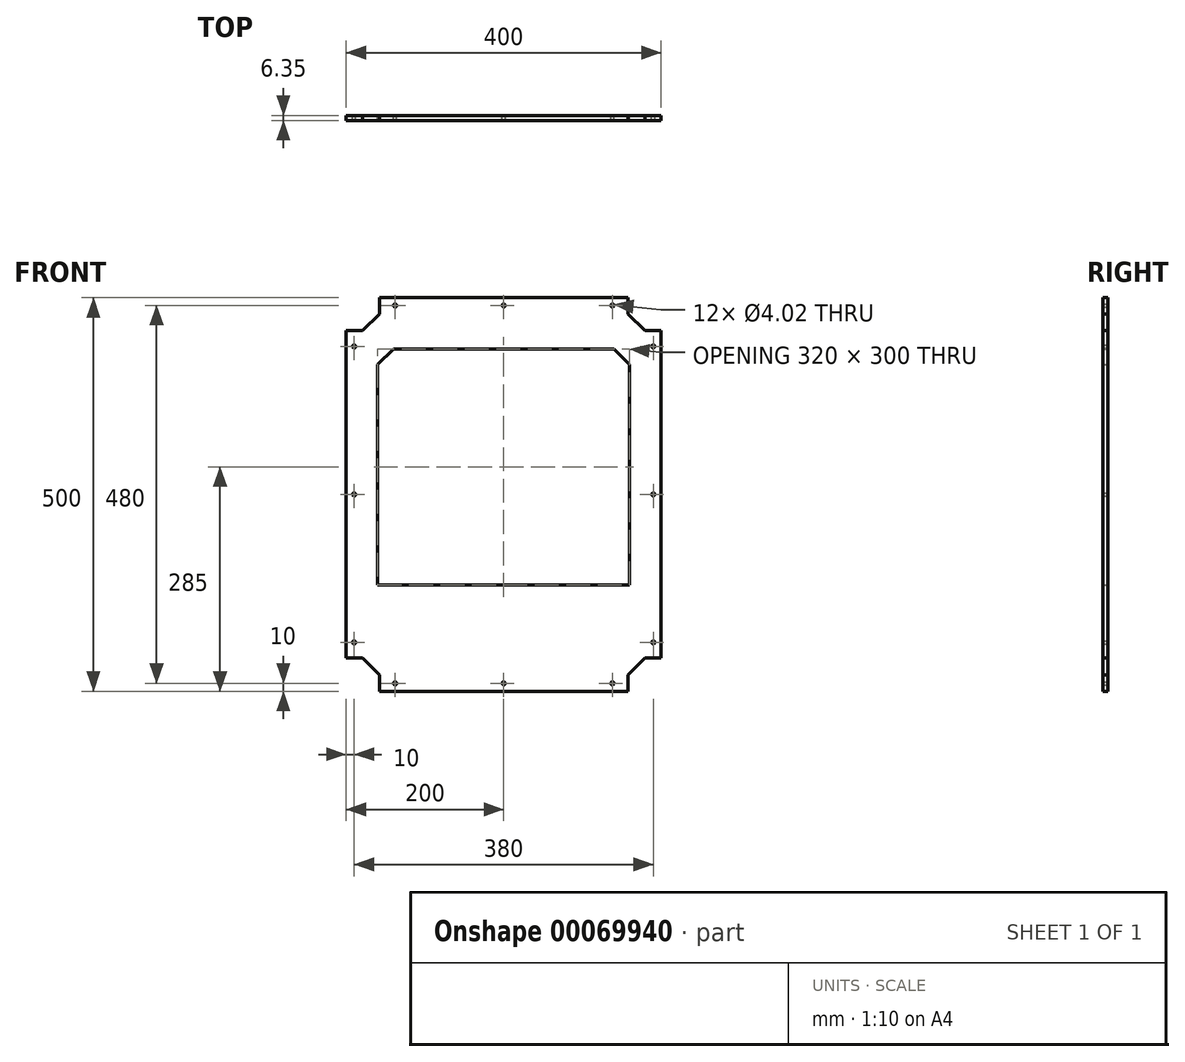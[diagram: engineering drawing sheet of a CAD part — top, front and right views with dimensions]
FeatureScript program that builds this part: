
annotation { "Feature Type Name" : "Feature", "Feature Type Description" : "" }
export const myFeature = defineFeature(function(context is Context, id is Id, definition is map)
    precondition{}
    {
        {
            var Q0;
            Q0=qCreatedBy(makeId("Front.planeOp"),FACE);
            var sketch = newSketch(context, id + "F0", { "sketchPlane" : qUnion([Q0])});
            skLineSegment(sketch, "E0", {"start": v(0, 0) * mm, "end": v(180, 0) * mm, "construction": true});
            skLineSegment(sketch, "E1", {"start": v(0, 0) * mm, "end": v(0, -230) * mm, "construction": true});
            skLineSegment(sketch, "E2", {"start": v(0, 0) * mm, "end": v(-180, 0) * mm, "construction": true});
            skLineSegment(sketch, "E3", {"start": v(0, 0) * mm, "end": v(0, 230) * mm, "construction": true});
            skLineSegment(sketch, "E4", {"start": v(0, 230) * mm, "end": v(160, 230) * mm, "construction": true});
            skLineSegment(sketch, "E5", {"start": v(0, 230) * mm, "end": v(-160, 230) * mm, "construction": true});
            skLineSegment(sketch, "E6", {"start": v(0, -230) * mm, "end": v(160, -230) * mm, "construction": true});
            skLineSegment(sketch, "E7", {"start": v(0, -230) * mm, "end": v(-160, -230) * mm, "construction": true});
            skLineSegment(sketch, "E8", {"start": v(-180, 0) * mm, "end": v(-180, -210) * mm, "construction": true});
            skLineSegment(sketch, "E9", {"start": v(-180, 0) * mm, "end": v(-180, 210) * mm, "construction": true});
            skLineSegment(sketch, "E10", {"start": v(180, 0) * mm, "end": v(180, 210) * mm, "construction": true});
            skLineSegment(sketch, "E11", {"start": v(180, 0) * mm, "end": v(180, -210) * mm, "construction": true});
            skLineSegment(sketch, "E12", {"start": v(-180, 210) * mm, "end": v(-160, 230) * mm, "construction": true});
            skLineSegment(sketch, "E13", {"start": v(160, 230) * mm, "end": v(180, 210) * mm, "construction": true});
            skLineSegment(sketch, "E14", {"start": v(-180, -210) * mm, "end": v(-160, -230) * mm, "construction": true});
            skLineSegment(sketch, "E15", {"start": v(160, -230) * mm, "end": v(180, -210) * mm, "construction": true});
            skLineSegment(sketch, "E16", {"start": v(140, 230) * mm, "end": v(140, 185) * mm, "construction": true});
            skLineSegment(sketch, "E17", {"start": v(140, 185) * mm, "end": v(180, 185) * mm, "construction": true});
            skLineSegment(sketch, "E18", {"start": v(-140, 230) * mm, "end": v(-140, 185) * mm, "construction": true});
            skLineSegment(sketch, "E19", {"start": v(-140, 185) * mm, "end": v(-180, 185) * mm, "construction": true});
            skLineSegment(sketch, "E20", {"start": v(170, 220) * mm, "end": v(168.59, 218.59) * mm, "construction": true});
            skLineSegment(sketch, "E21", {"start": v(180, 210) * mm, "end": v(200, 210) * mm, "construction": true});
            skLineSegment(sketch, "E22", {"start": v(190, 210) * mm, "end": v(190, 208) * mm, "construction": true});
            skLineSegment(sketch, "E23", {"start": v(160, 230) * mm, "end": v(160, 250) * mm, "construction": true});
            skLineSegment(sketch, "E24", {"start": v(180, -210) * mm, "end": v(200, -210) * mm, "construction": true});
            skLineSegment(sketch, "E25", {"start": v(160, -230) * mm, "end": v(160, -250) * mm, "construction": true});
            skLineSegment(sketch, "E26", {"start": v(-180, -210) * mm, "end": v(-200, -210) * mm, "construction": true});
            skLineSegment(sketch, "E27", {"start": v(-160, -230) * mm, "end": v(-160, -250) * mm, "construction": true});
            skLineSegment(sketch, "E28", {"start": v(190, -210) * mm, "end": v(190, -208) * mm, "construction": true});
            skLineSegment(sketch, "E29", {"start": v(160, -240) * mm, "end": v(158, -240) * mm, "construction": true});
            skLineSegment(sketch, "E30", {"start": v(190, -208) * mm, "end": v(200, -208) * mm});
            skLineSegment(sketch, "E31", {"start": v(170, -220) * mm, "end": v(168.59, -218.59) * mm, "construction": true});
            skLineSegment(sketch, "E32", {"start": v(190, -208) * mm, "end": v(179.17, -208) * mm});
            skLineSegment(sketch, "E33", {"start": v(168.59, -218.59) * mm, "end": v(179.17, -208) * mm});
            skLineSegment(sketch, "E34", {"start": v(168.59, -218.59) * mm, "end": v(158, -229.17) * mm});
            skLineSegment(sketch, "E35", {"start": v(158, -240) * mm, "end": v(158, -229.17) * mm});
            skLineSegment(sketch, "E36", {"start": v(158, -240) * mm, "end": v(158, -250) * mm});
            skLineSegment(sketch, "E37", {"start": v(200, -208) * mm, "end": v(200, 208) * mm});
            skLineSegment(sketch, "E38", {"start": v(200, 208) * mm, "end": v(190, 208) * mm});
            skLineSegment(sketch, "E39", {"start": v(190, 208) * mm, "end": v(179.17, 208) * mm});
            skLineSegment(sketch, "E40", {"start": v(168.59, 218.59) * mm, "end": v(179.17, 208) * mm});
            skLineSegment(sketch, "E41", {"start": v(168.59, 218.59) * mm, "end": v(158, 229.17) * mm});
            skLineSegment(sketch, "E42", {"start": v(160, 240) * mm, "end": v(158, 240) * mm, "construction": true});
            skPoint(sketch, "E42.endSnap0", {"position": v(160, 240) * mm});
            skLineSegment(sketch, "E43", {"start": v(158, 240) * mm, "end": v(158, 229.17) * mm});
            skLineSegment(sketch, "E44", {"start": v(-160, -240) * mm, "end": v(-158, -240) * mm, "construction": true});
            skLineSegment(sketch, "E45", {"start": v(-170, -220) * mm, "end": v(-168.59, -218.59) * mm, "construction": true});
            skLineSegment(sketch, "E46", {"start": v(-190, -210) * mm, "end": v(-190, -208) * mm, "construction": true});
            skPoint(sketch, "E46.endSnap0", {"position": v(-190, -210) * mm});
            skLineSegment(sketch, "E47", {"start": v(-168.59, -218.59) * mm, "end": v(-157.17, -230) * mm});
            skLineSegment(sketch, "E48", {"start": v(-158, -240) * mm, "end": v(-158, -229.17) * mm});
            skLineSegment(sketch, "E49", {"start": v(-190, -208) * mm, "end": v(-179.17, -208) * mm});
            skLineSegment(sketch, "E50", {"start": v(-168.59, -218.59) * mm, "end": v(-179.17, -208) * mm});
            skLineSegment(sketch, "E51", {"start": v(-158, -240) * mm, "end": v(-158, -250) * mm});
            skLineSegment(sketch, "E52", {"start": v(-190, -208) * mm, "end": v(-200, -208) * mm});
            skLineSegment(sketch, "E53", {"start": v(-158, -250) * mm, "end": v(158, -250) * mm});
            skLineSegment(sketch, "E54", {"start": v(-160, 230) * mm, "end": v(-160, 250) * mm, "construction": true});
            skLineSegment(sketch, "E55", {"start": v(-180, 210) * mm, "end": v(-200, 210) * mm, "construction": true});
            skLineSegment(sketch, "E56", {"start": v(-160, 240) * mm, "end": v(-158, 240) * mm, "construction": true});
            skLineSegment(sketch, "E57", {"start": v(-170, 220) * mm, "end": v(-168.59, 218.59) * mm, "construction": true});
            skLineSegment(sketch, "E58", {"start": v(-190, 210) * mm, "end": v(-190, 208) * mm, "construction": true});
            skLineSegment(sketch, "E59", {"start": v(-190, 208) * mm, "end": v(-200, 208) * mm});
            skLineSegment(sketch, "E60", {"start": v(-200, 208) * mm, "end": v(-200, -208) * mm});
            skLineSegment(sketch, "E61", {"start": v(-190, 208) * mm, "end": v(-179.17, 208) * mm});
            skLineSegment(sketch, "E62", {"start": v(-168.59, 218.59) * mm, "end": v(-179.17, 208) * mm});
            skLineSegment(sketch, "E63", {"start": v(-168.59, 218.59) * mm, "end": v(-158, 229.17) * mm});
            skLineSegment(sketch, "E64", {"start": v(-158, 240) * mm, "end": v(-158, 229.17) * mm});
            skLineSegment(sketch, "E65", {"start": v(-158, 240) * mm, "end": v(-158, 250) * mm});
            skLineSegment(sketch, "E66", {"start": v(-158, 250) * mm, "end": v(158, 250) * mm});
            skLineSegment(sketch, "E67", {"start": v(158, 250) * mm, "end": v(158, 240) * mm});
            skLineSegment(sketch, "E68", {"start": v(158, 240) * mm, "end": v(-158, 240) * mm, "construction": true});
            skLineSegment(sketch, "E69", {"start": v(-190, 208) * mm, "end": v(-190, -208) * mm, "construction": true});
            skLineSegment(sketch, "E70", {"start": v(-158, -240) * mm, "end": v(158, -240) * mm, "construction": true});
            skLineSegment(sketch, "E71", {"start": v(190, -208) * mm, "end": v(190, 208) * mm, "construction": true});
            skLineSegment(sketch, "E72", {"start": v(-168.59, 218.59) * mm, "end": v(-129.7, 179.7) * mm, "construction": true});
            skLineSegment(sketch, "E73", {"start": v(168.59, 218.59) * mm, "end": v(129.7, 179.7) * mm, "construction": true});
            skLineSegment(sketch, "E74", {"start": v(140, 185) * mm, "end": v(160, 165) * mm});
            skLineSegment(sketch, "E75", {"start": v(160, 165) * mm, "end": v(180, 165) * mm, "construction": true});
            skLineSegment(sketch, "E76", {"start": v(140, 185) * mm, "end": v(-140, 185) * mm});
            skLineSegment(sketch, "E77", {"start": v(-140, 185) * mm, "end": v(-160, 165) * mm});
            skLineSegment(sketch, "E78", {"start": v(-160, 165) * mm, "end": v(-180, 165) * mm, "construction": true});
            skLineSegment(sketch, "E79", {"start": v(-160, 165) * mm, "end": v(-160, -115) * mm});
            skLineSegment(sketch, "E80", {"start": v(0, -115) * mm, "end": v(-160, -115) * mm});
            skLineSegment(sketch, "E81", {"start": v(0, -115) * mm, "end": v(160, -115) * mm});
            skLineSegment(sketch, "E82", {"start": v(160, -115) * mm, "end": v(160, 165) * mm});
            skCircle(sketch, "E83", {"center": v(0, -240) * mm, "radius": 2 * mm});
            skCircle(sketch, "E84", {"center": v(138, -240) * mm, "radius": 2 * mm});
            skCircle(sketch, "E85", {"center": v(-138, -240) * mm, "radius": 2 * mm});
            skCircle(sketch, "E86", {"center": v(190, -188) * mm, "radius": 2 * mm});
            skCircle(sketch, "E87", {"center": v(190, 0) * mm, "radius": 2 * mm});
            skCircle(sketch, "E88", {"center": v(190, 188) * mm, "radius": 2 * mm});
            skCircle(sketch, "E89", {"center": v(0, 240) * mm, "radius": 2 * mm});
            skCircle(sketch, "E90", {"center": v(138, 240) * mm, "radius": 2 * mm});
            skCircle(sketch, "E91", {"center": v(-138, 240) * mm, "radius": 2 * mm});
            skCircle(sketch, "E92", {"center": v(-190, 188) * mm, "radius": 2 * mm});
            skCircle(sketch, "E93", {"center": v(-190, 0) * mm, "radius": 2 * mm});
            skCircle(sketch, "E94", {"center": v(-190, -188) * mm, "radius": 2 * mm});
            skSolve(sketch);
        }
        {
            var Q0;
            Q0=makeQuery(id+"F0.imprint","IMPRINT",FACE,{"disambiguationData":[TD([[makeQuery(id+"F0.imprint","IMPRINT",EDGE,{"derivedFrom":sQuery(id+"F0.wireOp",EDGE,"E30")}),1.0]])]});
            var Q1;
            Q1 = qSketchRegion(id + "F0", true);
            extrude(context, id + "F1", {"entities" : qUnion([Q0, Q1]), "depth" : 6.35 * mm});
        }
    });
